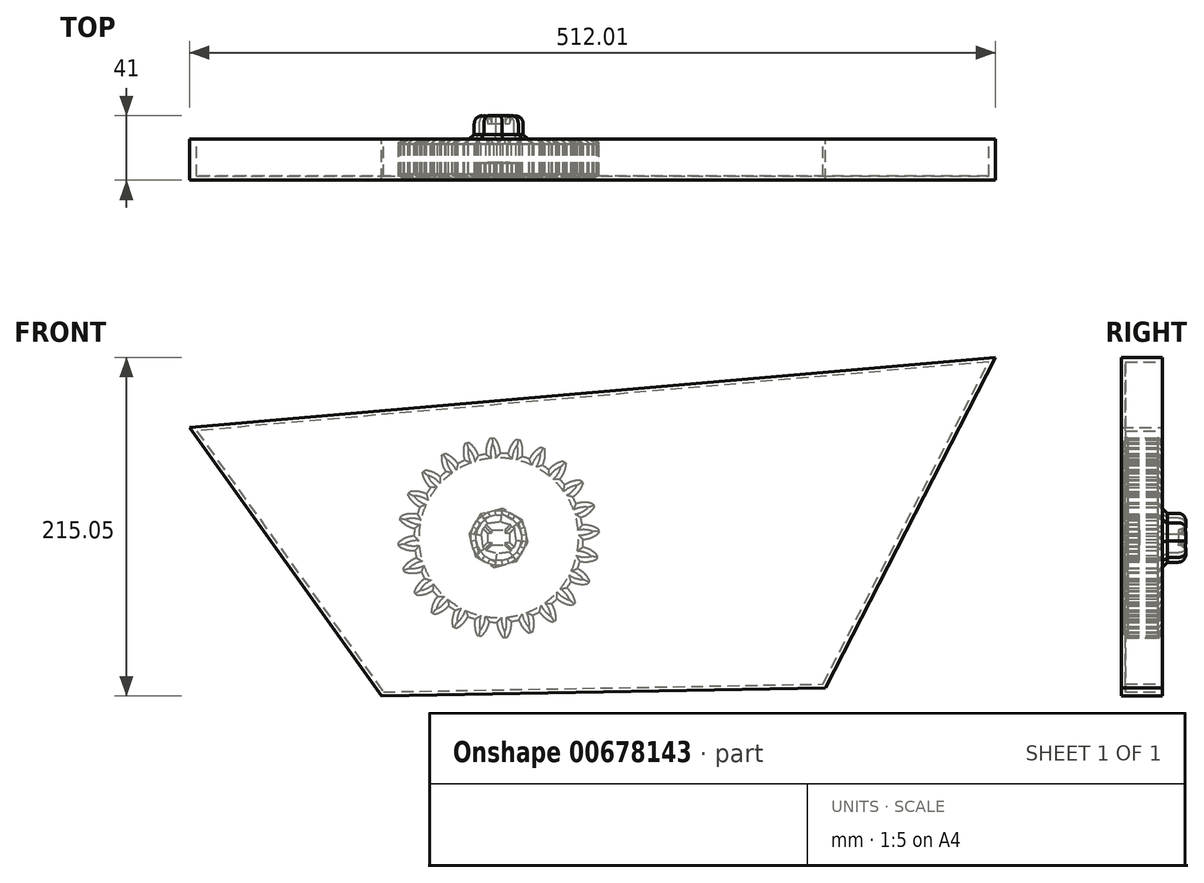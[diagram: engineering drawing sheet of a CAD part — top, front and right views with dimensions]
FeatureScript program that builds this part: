
annotation { "Feature Type Name" : "Feature", "Feature Type Description" : "" }
export const myFeature = defineFeature(function(context is Context, id is Id, definition is map)
    precondition{}
    {
        {
            var Q0;
            Q0=qCreatedBy(makeId("Front.planeOp"),FACE);
            var sketch = newSketch(context, id + "F0", { "sketchPlane" : qUnion([Q0])});
            skCircle(sketch, "E0", {"center": v(0, 0) * mm, "radius": 53.72 * mm});
            skCircle(sketch, "E1", {"center": v(0, 0) * mm, "radius": 58.67 * mm, "construction": true});
            skCircle(sketch, "E2", {"center": v(0, 0) * mm, "radius": 63.5 * mm, "construction": true});
            skLineSegment(sketch, "E3", {"start": v(0, 0) * mm, "end": v(0, 91.84) * mm, "construction": true});
            skLineSegment(sketch, "E4", {"start": v(0, 0) * mm, "end": v(-7.41, 113.09) * mm, "construction": true});
            skLineSegment(sketch, "E5", {"start": v(0, 58.67) * mm, "end": v(-83.5, 56.59) * mm, "construction": true});
            skLineSegment(sketch, "E6", {"start": v(0, 58.67) * mm, "end": v(-75.39, 29.08) * mm, "construction": true});
            skCircle(sketch, "E7", {"center": v(0, 0) * mm, "radius": 54.62 * mm, "construction": true});
            skCircle(sketch, "E8", {"center": v(0, 58.67) * mm, "radius": 16.52 * mm, "construction": true});
            skCircle(sketch, "E9", {"center": v(-15.38, 52.64) * mm, "radius": 16.52 * mm, "construction": true});
            skArc(sketch, "E10", {"start": v(0, 58.67) * mm, "mid": v(-1.21, 61.19) * mm, "end": v(-2.87, 63.43) * mm});
            skArc(sketch, "E11", {"start": v(1.1, 53.7) * mm, "mid": v(0.72, 56.23) * mm, "end": v(0, 58.67) * mm});
            skArc(sketch, "E12.MirrorCS", {"start": v(-8.1, 53.1) * mm, "mid": v(-8.06, 55.65) * mm, "end": v(-7.66, 58.17) * mm});
            skArc(sketch, "E13.MirrorCS", {"start": v(-7.66, 58.17) * mm, "mid": v(-6.78, 60.82) * mm, "end": v(-5.43, 63.27) * mm});
            skArc(sketch, "E14", {"start": v(-2.87, 63.43) * mm, "mid": v(-4.17, 63.55) * mm, "end": v(-5.43, 63.27) * mm});
            skCircle(sketch, "E15.cCircle", {"center": v(0, 0) * mm, "radius": 14.46 * mm, "construction": true});
            skLineSegment(sketch, "E15.0", {"start": v(-15.51, 2.1) * mm, "end": v(-9.48, 12.46) * mm});
            skLineSegment(sketch, "E15.1", {"start": v(-9.48, 12.46) * mm, "end": v(2.1, 15.51) * mm});
            skLineSegment(sketch, "E15.2", {"start": v(2.1, 15.51) * mm, "end": v(12.46, 9.48) * mm});
            skLineSegment(sketch, "E15.3", {"start": v(12.46, 9.48) * mm, "end": v(15.51, -2.1) * mm});
            skLineSegment(sketch, "E15.4", {"start": v(15.51, -2.1) * mm, "end": v(9.48, -12.46) * mm});
            skLineSegment(sketch, "E15.5", {"start": v(9.48, -12.46) * mm, "end": v(-2.1, -15.51) * mm});
            skLineSegment(sketch, "E15.6", {"start": v(-2.1, -15.51) * mm, "end": v(-12.46, -9.48) * mm});
            skLineSegment(sketch, "E15.7", {"start": v(-12.46, -9.48) * mm, "end": v(-15.51, 2.1) * mm});
            skPoint(sketch, "E15.0.midPoint", {"position": v(-12.5, 7.28) * mm});
            skLineSegment(sketch, "E16.bottom", {"start": v(-4.6, 5.04) * mm, "end": v(4, 5.04) * mm});
            skLineSegment(sketch, "E16.top", {"start": v(-4.6, -4.7) * mm, "end": v(4, -4.7) * mm});
            skLineSegment(sketch, "E16.left", {"start": v(-4.6, 5.04) * mm, "end": v(-4.6, -4.7) * mm});
            skLineSegment(sketch, "E16.right", {"start": v(4, 5.04) * mm, "end": v(4, -4.7) * mm});
            skLineSegment(sketch, "E17.bottom", {"start": v(-7.04, 2.93) * mm, "end": v(6.93, 2.93) * mm});
            skLineSegment(sketch, "E17.top", {"start": v(-7.04, -2.92) * mm, "end": v(6.93, -2.92) * mm});
            skLineSegment(sketch, "E17.left", {"start": v(-7.04, 2.93) * mm, "end": v(-7.04, -2.92) * mm});
            skLineSegment(sketch, "E17.right", {"start": v(6.93, 2.93) * mm, "end": v(6.93, -2.92) * mm});
            skSolve(sketch);
        }
        {
            var Q0;
            {var subQ0=sQuery(id+"F0.wireOp",EDGE,"E0");var subQ1=makeQuery(id+"F0.imprint","INTERSECT",VERTEX,{"derivedFrom":[subQ0,sQuery(id+"F0.wireOp",EDGE,"E11")]});Q0=makeQuery(id+"F0.imprint","IMPRINT",FACE,{"disambiguationData":[TD([[makeQuery(id+"F0.imprint","IMPRINT",EDGE,{"disambiguationData":[TD([[subQ1,-1.0]])],"derivedFrom":subQ0}),1.0]])]});}
            var Q1;
            Q1=makeQuery(id+"F0.imprint","IMPRINT",FACE,{"disambiguationData":[TD([[makeQuery(id+"F0.imprint","IMPRINT",EDGE,{"derivedFrom":sQuery(id+"F0.wireOp",EDGE,"E10")}),1.0]])]});
            extrude(context, id + "F1", {"entities" : qUnion([Q0, Q1]), "depth" : 25 * mm, "offsetDistance" : 25 * mm});
        }
        {
            var Q0;
            Q0=makeQuery(id+"F1.opExtrude","SWEPT_BODY",BODY,{"disambiguationData":[OSD([sQuery(id+"F0.wireOp",EDGE,"E0"),sQuery(id+"F0.wireOp",EDGE,"E10"),sQuery(id+"F0.wireOp",EDGE,"E11"),sQuery(id+"F0.wireOp",EDGE,"E12.MirrorCS"),sQuery(id+"F0.wireOp",EDGE,"E13.MirrorCS"),sQuery(id+"F0.wireOp",EDGE,"E14")])]});
            var Q1;
            Q1=makeQuery(id+"F1.opExtrude","SWEPT_FACE",FACE,{"disambiguationData":[OSD([sQuery(id+"F0.wireOp",EDGE,"E0")])]});
            circularPattern(context, id + "F2", {"entities" : qUnion([Q0]), "axis" : qUnion([Q1]), "angle" : 360 * degree, "instanceCount" : 24, "equalSpace" : true});
        }
        {
            var Q0;
            Q0=makeQuery(id+"F0.imprint","IMPRINT",FACE,{"disambiguationData":[TD([[makeQuery(id+"F0.imprint","IMPRINT",EDGE,{"derivedFrom":sQuery(id+"F0.wireOp",EDGE,"E15.0")}),-1.0]])]});
            extrude(context, id + "F3", {"entities" : qUnion([Q0]), "operationType" : NewBodyOperationType.ADD, "endBound" : BoundingType.SYMMETRIC, "oppositeDirection" : true, "depth" : 30 * mm, "offsetDistance" : 25 * mm});
        }
        {
            var Q0;
            Q0=makeQuery(id+"F3.opExtrude","CAP_FACE",FACE,{"disambiguationData":[OSD([sQuery(id+"F0.wireOp",EDGE,"E15.0"),sQuery(id+"F0.wireOp",EDGE,"E15.1"),sQuery(id+"F0.wireOp",EDGE,"E15.2"),sQuery(id+"F0.wireOp",EDGE,"E15.3"),sQuery(id+"F0.wireOp",EDGE,"E15.4"),sQuery(id+"F0.wireOp",EDGE,"E15.5"),sQuery(id+"F0.wireOp",EDGE,"E15.6"),sQuery(id+"F0.wireOp",EDGE,"E15.7"),sQuery(id+"F0.wireOp",EDGE,"E16.bottom"),sQuery(id+"F0.wireOp",EDGE,"E16.top"),sQuery(id+"F0.wireOp",EDGE,"E16.left"),sQuery(id+"F0.wireOp",EDGE,"E16.right"),sQuery(id+"F0.wireOp",EDGE,"E17.bottom"),sQuery(id+"F0.wireOp",EDGE,"E17.top"),sQuery(id+"F0.wireOp",EDGE,"E17.left"),sQuery(id+"F0.wireOp",EDGE,"E17.right")])],"isStart":false});
            fillet(context, id + "F4", {"entities" : qUnion([Q0]), "radius" : 5 * mm, "tangentPropagation" : true, "allowEdgeOverflow" : false});
        }
        {
            var Q0;
            {var subQ0=makeQuery(id+"F1.opExtrude","CAP_FACE",FACE,{"disambiguationData":[OSD([sQuery(id+"F0.wireOp",EDGE,"E0"),sQuery(id+"F0.wireOp",EDGE,"E10"),sQuery(id+"F0.wireOp",EDGE,"E11"),sQuery(id+"F0.wireOp",EDGE,"E12.MirrorCS"),sQuery(id+"F0.wireOp",EDGE,"E13.MirrorCS"),sQuery(id+"F0.wireOp",EDGE,"E14"),sQuery(id+"F0.wireOp",EDGE,"E15.0"),sQuery(id+"F0.wireOp",EDGE,"E15.1"),sQuery(id+"F0.wireOp",EDGE,"E15.2"),sQuery(id+"F0.wireOp",EDGE,"E15.3"),sQuery(id+"F0.wireOp",EDGE,"E15.4"),sQuery(id+"F0.wireOp",EDGE,"E15.5"),sQuery(id+"F0.wireOp",EDGE,"E15.6"),sQuery(id+"F0.wireOp",EDGE,"E15.7")])],"isStart":true});Q0=makeQuery(id+"F3.boolean.opBoolean","MERGE",FACE,{"derivedFrom":[subQ0,makeQuery(id+"F2.opPattern","COPY",FACE,{"derivedFrom":subQ0,"instanceName":"1"}),makeQuery(id+"F2.opPattern","COPY",FACE,{"derivedFrom":subQ0,"instanceName":"2"}),makeQuery(id+"F2.opPattern","COPY",FACE,{"derivedFrom":subQ0,"instanceName":"3"}),makeQuery(id+"F2.opPattern","COPY",FACE,{"derivedFrom":subQ0,"instanceName":"4"}),makeQuery(id+"F2.opPattern","COPY",FACE,{"derivedFrom":subQ0,"instanceName":"5"}),makeQuery(id+"F2.opPattern","COPY",FACE,{"derivedFrom":subQ0,"instanceName":"6"}),makeQuery(id+"F2.opPattern","COPY",FACE,{"derivedFrom":subQ0,"instanceName":"7"}),makeQuery(id+"F2.opPattern","COPY",FACE,{"derivedFrom":subQ0,"instanceName":"8"}),makeQuery(id+"F2.opPattern","COPY",FACE,{"derivedFrom":subQ0,"instanceName":"9"}),makeQuery(id+"F2.opPattern","COPY",FACE,{"derivedFrom":subQ0,"instanceName":"10"}),makeQuery(id+"F2.opPattern","COPY",FACE,{"derivedFrom":subQ0,"instanceName":"11"}),makeQuery(id+"F2.opPattern","COPY",FACE,{"derivedFrom":subQ0,"instanceName":"12"}),makeQuery(id+"F2.opPattern","COPY",FACE,{"derivedFrom":subQ0,"instanceName":"13"}),makeQuery(id+"F2.opPattern","COPY",FACE,{"derivedFrom":subQ0,"instanceName":"14"}),makeQuery(id+"F2.opPattern","COPY",FACE,{"derivedFrom":subQ0,"instanceName":"15"}),makeQuery(id+"F2.opPattern","COPY",FACE,{"derivedFrom":subQ0,"instanceName":"16"}),makeQuery(id+"F2.opPattern","COPY",FACE,{"derivedFrom":subQ0,"instanceName":"17"}),makeQuery(id+"F2.opPattern","COPY",FACE,{"derivedFrom":subQ0,"instanceName":"18"}),makeQuery(id+"F2.opPattern","COPY",FACE,{"derivedFrom":subQ0,"instanceName":"19"}),makeQuery(id+"F2.opPattern","COPY",FACE,{"derivedFrom":subQ0,"instanceName":"20"}),makeQuery(id+"F2.opPattern","COPY",FACE,{"derivedFrom":subQ0,"instanceName":"21"}),makeQuery(id+"F2.opPattern","COPY",FACE,{"derivedFrom":subQ0,"instanceName":"22"}),makeQuery(id+"F2.opPattern","COPY",FACE,{"derivedFrom":subQ0,"instanceName":"23"})]});}
            chamfer(context, id + "F5", {"entities" : qUnion([Q0]), "width" : 3 * mm, "tangentPropagation" : true});
        }
        {
            var Q0;
            {var subQ0=makeQuery(id+"F1.opExtrude","CAP_FACE",FACE,{"disambiguationData":[OSD([sQuery(id+"F0.wireOp",EDGE,"E0"),sQuery(id+"F0.wireOp",EDGE,"E10"),sQuery(id+"F0.wireOp",EDGE,"E11"),sQuery(id+"F0.wireOp",EDGE,"E12.MirrorCS"),sQuery(id+"F0.wireOp",EDGE,"E13.MirrorCS"),sQuery(id+"F0.wireOp",EDGE,"E14"),sQuery(id+"F0.wireOp",EDGE,"E15.0"),sQuery(id+"F0.wireOp",EDGE,"E15.1"),sQuery(id+"F0.wireOp",EDGE,"E15.2"),sQuery(id+"F0.wireOp",EDGE,"E15.3"),sQuery(id+"F0.wireOp",EDGE,"E15.4"),sQuery(id+"F0.wireOp",EDGE,"E15.5"),sQuery(id+"F0.wireOp",EDGE,"E15.6"),sQuery(id+"F0.wireOp",EDGE,"E15.7")])],"isStart":false});Q0=makeQuery(id+"F3.boolean.opBoolean","MERGE",FACE,{"derivedFrom":[subQ0,makeQuery(id+"F2.opPattern","COPY",FACE,{"derivedFrom":subQ0,"instanceName":"1"}),makeQuery(id+"F2.opPattern","COPY",FACE,{"derivedFrom":subQ0,"instanceName":"2"}),makeQuery(id+"F2.opPattern","COPY",FACE,{"derivedFrom":subQ0,"instanceName":"3"}),makeQuery(id+"F2.opPattern","COPY",FACE,{"derivedFrom":subQ0,"instanceName":"4"}),makeQuery(id+"F2.opPattern","COPY",FACE,{"derivedFrom":subQ0,"instanceName":"5"}),makeQuery(id+"F2.opPattern","COPY",FACE,{"derivedFrom":subQ0,"instanceName":"6"}),makeQuery(id+"F2.opPattern","COPY",FACE,{"derivedFrom":subQ0,"instanceName":"7"}),makeQuery(id+"F2.opPattern","COPY",FACE,{"derivedFrom":subQ0,"instanceName":"8"}),makeQuery(id+"F2.opPattern","COPY",FACE,{"derivedFrom":subQ0,"instanceName":"9"}),makeQuery(id+"F2.opPattern","COPY",FACE,{"derivedFrom":subQ0,"instanceName":"10"}),makeQuery(id+"F2.opPattern","COPY",FACE,{"derivedFrom":subQ0,"instanceName":"11"}),makeQuery(id+"F2.opPattern","COPY",FACE,{"derivedFrom":subQ0,"instanceName":"12"}),makeQuery(id+"F2.opPattern","COPY",FACE,{"derivedFrom":subQ0,"instanceName":"13"}),makeQuery(id+"F2.opPattern","COPY",FACE,{"derivedFrom":subQ0,"instanceName":"14"}),makeQuery(id+"F2.opPattern","COPY",FACE,{"derivedFrom":subQ0,"instanceName":"15"}),makeQuery(id+"F2.opPattern","COPY",FACE,{"derivedFrom":subQ0,"instanceName":"16"}),makeQuery(id+"F2.opPattern","COPY",FACE,{"derivedFrom":subQ0,"instanceName":"17"}),makeQuery(id+"F2.opPattern","COPY",FACE,{"derivedFrom":subQ0,"instanceName":"18"}),makeQuery(id+"F2.opPattern","COPY",FACE,{"derivedFrom":subQ0,"instanceName":"19"}),makeQuery(id+"F2.opPattern","COPY",FACE,{"derivedFrom":subQ0,"instanceName":"20"}),makeQuery(id+"F2.opPattern","COPY",FACE,{"derivedFrom":subQ0,"instanceName":"21"}),makeQuery(id+"F2.opPattern","COPY",FACE,{"derivedFrom":subQ0,"instanceName":"22"}),makeQuery(id+"F2.opPattern","COPY",FACE,{"derivedFrom":subQ0,"instanceName":"23"})]});}
            chamfer(context, id + "F6", {"entities" : qUnion([Q0]), "width" : 3 * mm, "tangentPropagation" : true});
        }
        {
            var Q0;
            {var subQ0=sQuery(id+"F0.wireOp",EDGE,"E17.bottom");var subQ1=sQuery(id+"F0.wireOp",EDGE,"E16.left");var subQ2=makeQuery(id+"F0.imprint","INTERSECT",VERTEX,{"derivedFrom":[subQ1,subQ0]});Q0=makeQuery(id+"F0.imprint","IMPRINT",FACE,{"disambiguationData":[TD([[makeQuery(id+"F0.imprint","IMPRINT",EDGE,{"disambiguationData":[TD([[subQ2,-1.0]])],"derivedFrom":subQ1}),1.0]])]});}
            var Q1;
            {var subQ0=sQuery(id+"F0.wireOp",EDGE,"E16.top");Q1=makeQuery(id+"F0.imprint","IMPRINT",FACE,{"disambiguationData":[TD([[makeQuery(id+"F0.imprint","IMPRINT",EDGE,{"derivedFrom":subQ0}),1.0]])]});}
            var Q2;
            {var subQ5=sQuery(id+"F0.wireOp",EDGE,"E17.left");Q2=makeQuery(id+"F0.imprint","IMPRINT",FACE,{"disambiguationData":[TD([[makeQuery(id+"F0.imprint","IMPRINT",EDGE,{"derivedFrom":subQ5}),1.0]])]});}
            var Q3;
            {var subQ0=sQuery(id+"F0.wireOp",EDGE,"E16.bottom");Q3=makeQuery(id+"F0.imprint","IMPRINT",FACE,{"disambiguationData":[TD([[makeQuery(id+"F0.imprint","IMPRINT",EDGE,{"derivedFrom":subQ0}),-1.0]])]});}
            var Q4;
            {var subQ5=sQuery(id+"F0.wireOp",EDGE,"E17.right");Q4=makeQuery(id+"F0.imprint","IMPRINT",FACE,{"disambiguationData":[TD([[makeQuery(id+"F0.imprint","IMPRINT",EDGE,{"derivedFrom":subQ5}),-1.0]])]});}
            extrude(context, id + "F7", {"entities" : qUnion([Q0, Q1, Q2, Q3, Q4]), "operationType" : NewBodyOperationType.ADD, "endBound" : BoundingType.SYMMETRIC, "oppositeDirection" : true, "depth" : 29 * mm, "offsetDistance" : 25 * mm});
        }
        {
            var Q0;
            Q0=qCreatedBy(makeId("Front.planeOp"),FACE);
            var sketch = newSketch(context, id + "F8", { "sketchPlane" : qUnion([Q0])});
            skLineSegment(sketch, "E18", {"start": v(-196.45, 70.07) * mm, "end": v(-74.44, -100.41) * mm});
            skLineSegment(sketch, "E19", {"start": v(-74.44, -100.41) * mm, "end": v(207.47, -95.4) * mm});
            skLineSegment(sketch, "E20", {"start": v(207.47, -95.4) * mm, "end": v(315.56, 114.64) * mm});
            skLineSegment(sketch, "E21", {"start": v(315.56, 114.64) * mm, "end": v(-196.45, 70.07) * mm});
            skSolve(sketch);
        }
        {
            var Q0;
            Q0=makeQuery(id+"F8.imprint","IMPRINT",FACE,{"disambiguationData":[TD([[makeQuery(id+"F8.imprint","IMPRINT",EDGE,{"derivedFrom":sQuery(id+"F8.wireOp",EDGE,"E18")}),1.0]])]});
            extrude(context, id + "F9", {"entities" : qUnion([Q0]), "depth" : 26 * mm, "offsetDistance" : 25 * mm});
        }
        {
            var Q0;
            Q0=makeQuery(id+"F9.opExtrude","CAP_FACE",FACE,{"disambiguationData":[OSD([sQuery(id+"F8.wireOp",EDGE,"E18"),sQuery(id+"F8.wireOp",EDGE,"E19"),sQuery(id+"F8.wireOp",EDGE,"E20"),sQuery(id+"F8.wireOp",EDGE,"E21")])],"isStart":true});
            shell(context, id + "F10", {"entities" : qUnion([Q0]), "thickness" : 2.5 * mm});
        }
    });
